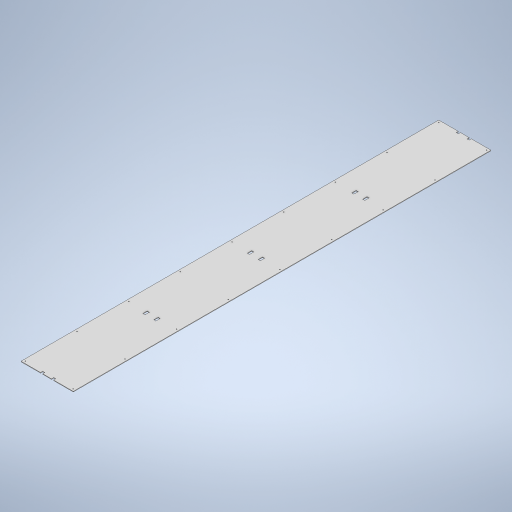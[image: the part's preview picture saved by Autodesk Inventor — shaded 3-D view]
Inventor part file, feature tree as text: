
AUTODESK INVENTOR PART (.ipt)
format: ipt  version: 2023 (Build 270158030, 158C)  size: 321,024 bytes
history: native  units: in
note: dims shown in document units (in); Inventor stores cm internally (conversion verified against a paired STEP export)
features: extrude x1
ambient origin geometry x8: Origin, YZ Plane, XZ Plane, XY Plane, X Axis, Y Axis, Z Axis, Center Point
bodies: Solid1 (feature_tree)
feature tree (1):
  extrude  "Extrusion1"  Depth=12.0in
